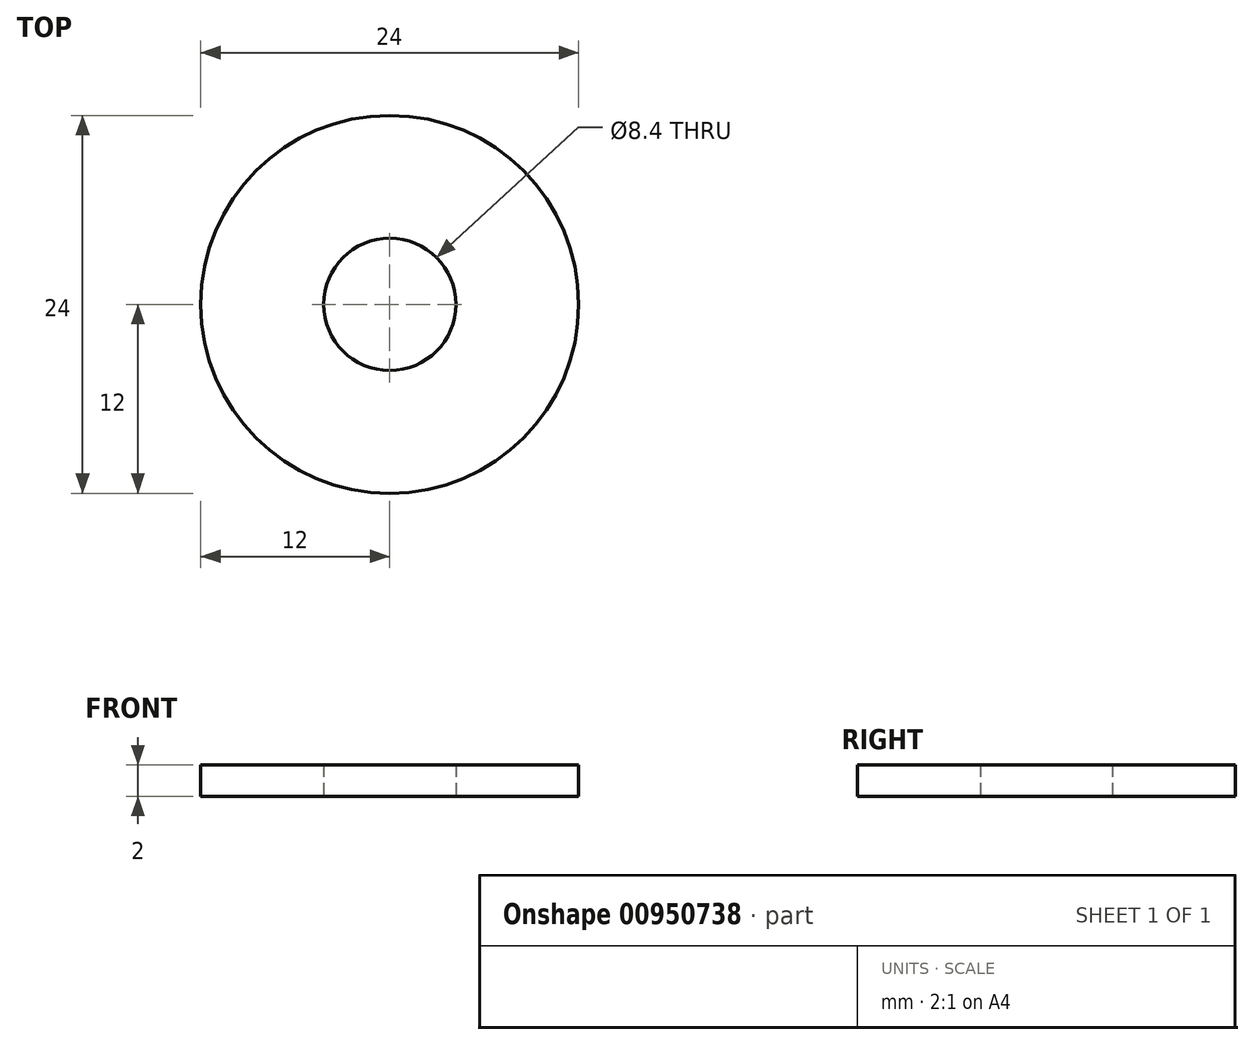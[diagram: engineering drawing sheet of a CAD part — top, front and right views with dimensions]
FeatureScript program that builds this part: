
annotation { "Feature Type Name" : "Feature", "Feature Type Description" : "" }
export const myFeature = defineFeature(function(context is Context, id is Id, definition is map)
    precondition{}
    {
        {
            var Q0;
            Q0=qCreatedBy(makeId("Top.planeOp"),FACE);
            var sketch = newSketch(context, id + "F0", { "sketchPlane" : qUnion([Q0])});
            skCircle(sketch, "E0", {"center": v(0, 0) * mm, "radius": 12 * mm});
            skCircle(sketch, "E1", {"center": v(0, 0) * mm, "radius": 4.2 * mm});
            skSolve(sketch);
        }
        {
            var Q0;
            Q0=qSketchRegion(id+"F0",true);
            extrude(context, id + "F1", {"entities" : qUnion([Q0]), "depth" : 2 * mm, "offsetDistance" : 25 * mm});
        }
    });
